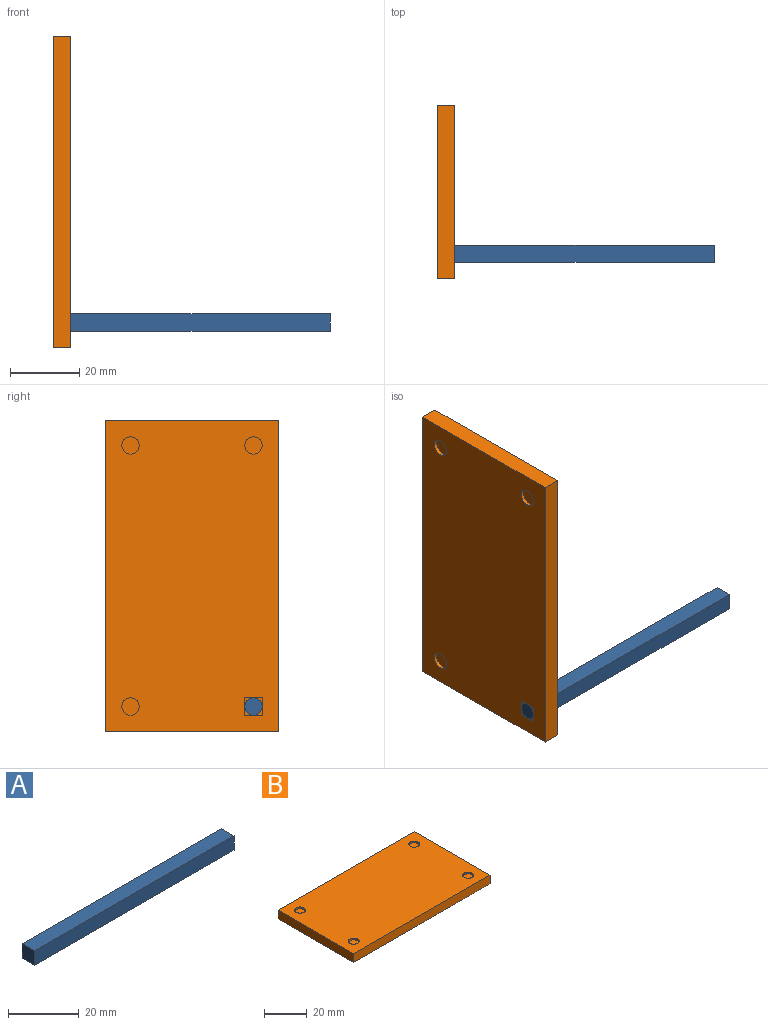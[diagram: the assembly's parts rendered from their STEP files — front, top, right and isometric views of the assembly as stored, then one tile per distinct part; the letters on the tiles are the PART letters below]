
ASSEMBLY  parts=2 mates=1
PART A: 6 faces, bbox 80x5x5 mm
  f0: plane 80x5mm, normal (0,1,0), area 400mm2, adj f1,f3,f4,f5
  f1: plane 5x5mm, normal (-1,0,0), area 25mm2, adj f0,f2,f4,f5
  f2: plane 80x5mm, normal (0,-1,0), area 400mm2, adj f1,f3,f4,f5
  f3: plane 5x5mm, normal (1,0,0), area 25mm2, adj f0,f2,f4,f5
  f4: plane 80x5mm, normal (0,0,1), area 400mm2, adj f0,f1,f2,f3
  f5: plane 80x5mm, normal (0,0,-1), area 400mm2, adj f0,f1,f2,f3
PART B: 14 faces, bbox 90x50x5 mm
  f0: plane 90x50mm, normal (0,0,1), area 4421.5mm2, adj f1,f2,f3,f4,f6,f8,f10,f12
  f1: plane 90x5mm, normal (0,-1,0), area 450mm2, adj f0,f2,f4,f5
  f2: plane 50x5mm, normal (1,0,0), area 250mm2, adj f0,f1,f3,f5
  f3: plane 90x5mm, normal (0,1,0), area 450mm2, adj f0,f2,f4,f5
  f4: plane 50x5mm, normal (-1,0,0), area 250mm2, adj f0,f1,f3,f5
  f5: plane 90x50mm, normal (0,0,-1), area 4500mm2, adj f1,f2,f3,f4
  f6: cylinder r=2.5mm len=5mm, axis (0,0,1), area 15.7mm2, adj f0,f7
  f7: plane 5x5mm, normal (0,0,1), area 19.6mm2, adj f6
  f8: cylinder r=2.5mm len=5mm, axis (0,0,1), area 15.7mm2, adj f0,f9
  f9: plane 5x5mm, normal (0,0,1), area 19.6mm2, adj f8
  f10: cylinder r=2.5mm len=5mm, axis (0,0,1), area 15.7mm2, adj f0,f11
  f11: plane 5x5mm, normal (0,0,1), area 19.6mm2, adj f10
  f12: cylinder r=2.5mm len=5mm, axis (0,0,1), area 15.7mm2, adj f0,f13
  f13: plane 5x5mm, normal (0,0,1), area 19.6mm2, adj f12
PLACE A t=(-9.43,35.09,-14.99)mm
PLACE B rot(axis=(0,-1,0),90deg) t=(-43.85,4.33,25.23)mm
MATE fastened B.f10 <-> A.f1  axis (-1,0,0) through (-48.85,-13.43,-12.49)mm
